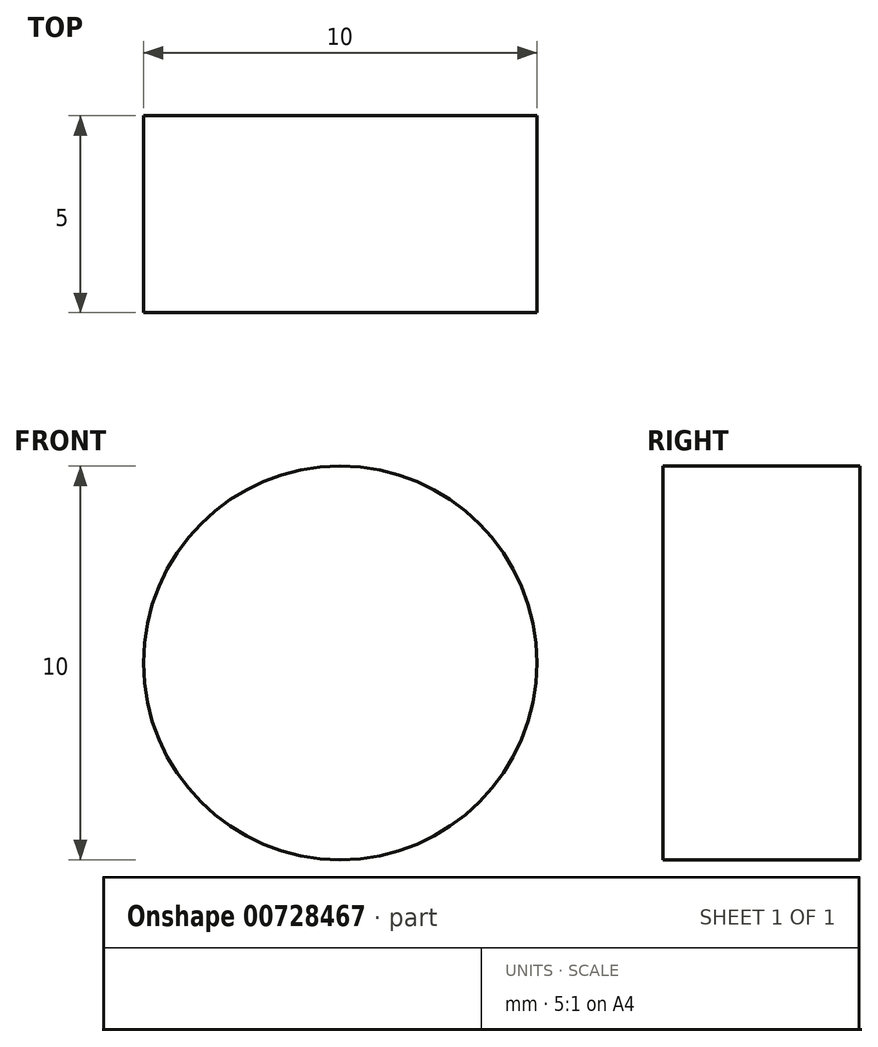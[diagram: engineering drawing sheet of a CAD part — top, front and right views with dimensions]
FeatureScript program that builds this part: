
annotation { "Feature Type Name" : "Feature", "Feature Type Description" : "" }
export const myFeature = defineFeature(function(context is Context, id is Id, definition is map)
    precondition{}
    {
        {
            var Q0;
            Q0=qCreatedBy(makeId("Front.planeOp"),FACE);
            var sketch = newSketch(context, id + "F0", { "sketchPlane" : qUnion([Q0])});
            skCircle(sketch, "E0", {"center": v(0, 0) * mm, "radius": 5 * mm});
            skSolve(sketch);
        }
        {
            var Q0;
            Q0=makeQuery(id+"F0.imprint","IMPRINT",FACE,{"disambiguationData":[TD([[makeQuery(id+"F0.imprint","IMPRINT",EDGE,{"derivedFrom":sQuery(id+"F0.wireOp",EDGE,"E0")}),1.0]])]});
            extrude(context, id + "F1", {"entities" : qUnion([Q0]), "depth" : 5 * mm, "offsetDistance" : 25 * mm});
        }
    });
